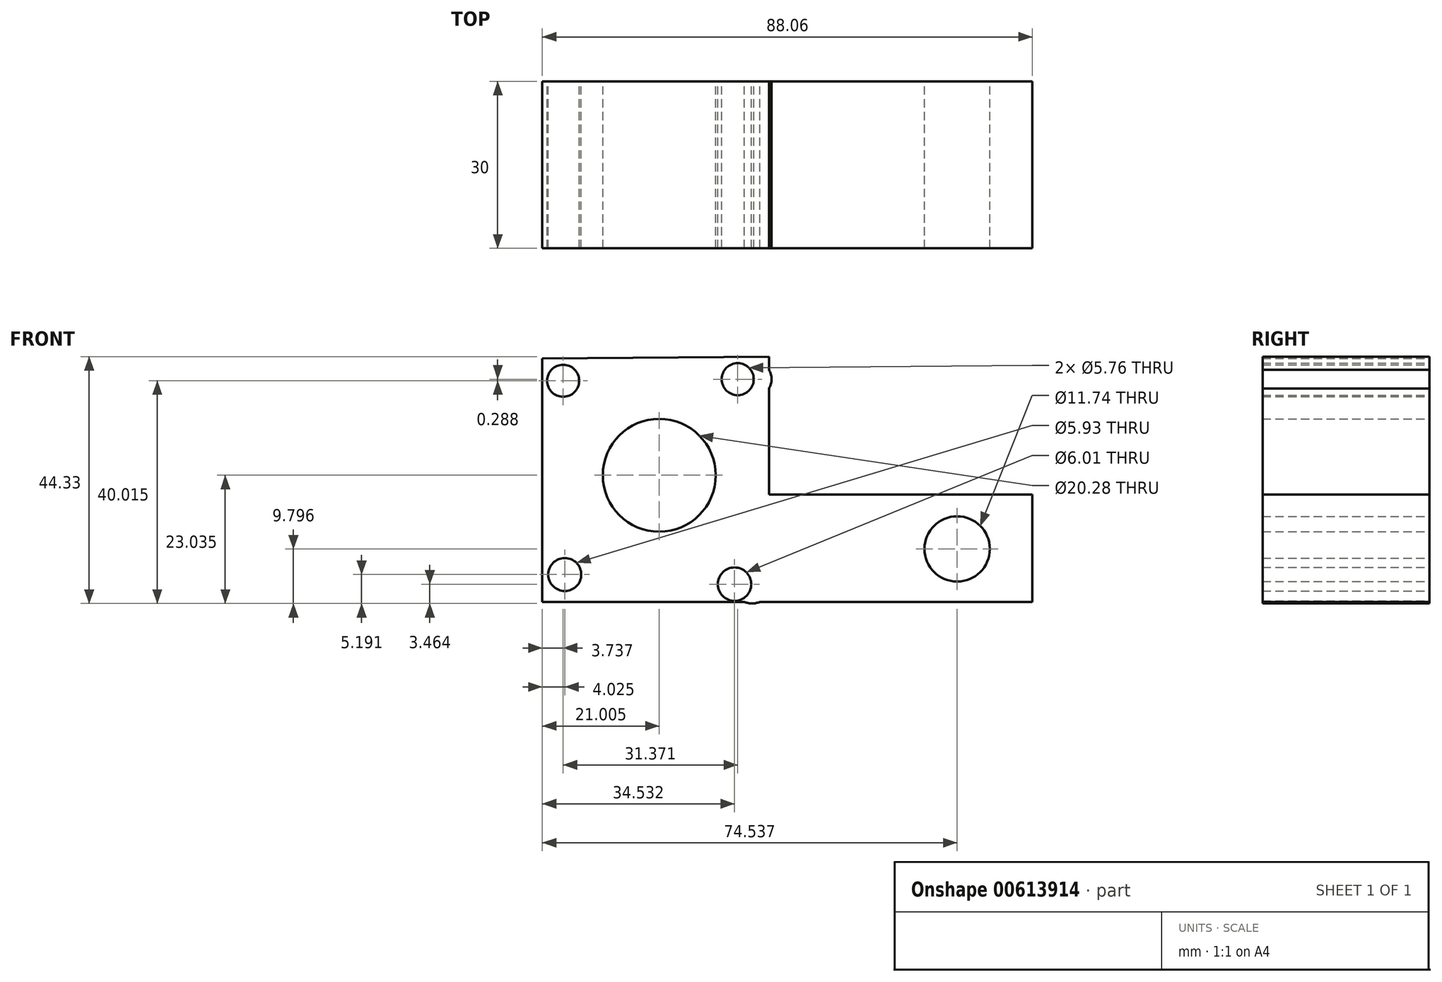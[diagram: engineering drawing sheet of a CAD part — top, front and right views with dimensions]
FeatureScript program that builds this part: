
annotation { "Feature Type Name" : "Feature", "Feature Type Description" : "" }
export const myFeature = defineFeature(function(context is Context, id is Id, definition is map)
    precondition{}
    {
        {
            var Q0;
            Q0=qCreatedBy(makeId("Front.planeOp"),FACE);
            var sketch = newSketch(context, id + "F0", { "sketchPlane" : qUnion([Q0])});
            skLineSegment(sketch, "E0", {"start": v(-40.72, 17.12) * mm, "end": v(-40.72, -26.62) * mm});
            skLineSegment(sketch, "E1", {"start": v(-40.72, -26.62) * mm, "end": v(47.34, -26.62) * mm});
            skLineSegment(sketch, "E2", {"start": v(47.34, -26.62) * mm, "end": v(47.34, -7.34) * mm});
            skLineSegment(sketch, "E3", {"start": v(47.34, -7.34) * mm, "end": v(0, -7.34) * mm});
            skLineSegment(sketch, "E4", {"start": v(0, -7.34) * mm, "end": v(0, 17.41) * mm});
            skLineSegment(sketch, "E5", {"start": v(0, 17.41) * mm, "end": v(-40.72, 17.12) * mm});
            skCircle(sketch, "E6", {"center": v(-19.71, -3.89) * mm, "radius": 10.14 * mm});
            skCircle(sketch, "E7", {"center": v(33.82, -17.12) * mm, "radius": 5.87 * mm});
            skCircle(sketch, "E8", {"center": v(-36.98, 13.1) * mm, "radius": 2.88 * mm});
            skArc(sketch, "E9", {"start": v(0, 11.69) * mm, "mid": v(0.48, 13.38) * mm, "end": v(0, 15.08) * mm});
            skCircle(sketch, "E10", {"center": v(-36.7, -21.73) * mm, "radius": 2.96 * mm});
            skArc(sketch, "E11", {"start": v(-4.43, -26.62) * mm, "mid": v(-3.02, -26.92) * mm, "end": v(-1.61, -26.62) * mm});
            skCircle(sketch, "E12", {"center": v(-5.61, 13.38) * mm, "radius": 2.88 * mm});
            skCircle(sketch, "E13", {"center": v(-6.19, -23.46) * mm, "radius": 3 * mm});
            skSolve(sketch);
        }
        {
            var Q0;
            Q0 = qSketchRegion(id + "F0", true);
            extrude(context, id + "F1", {"entities" : qUnion([Q0]), "depth" : 30 * mm, "offsetDistance" : 25 * mm});
        }
    });
